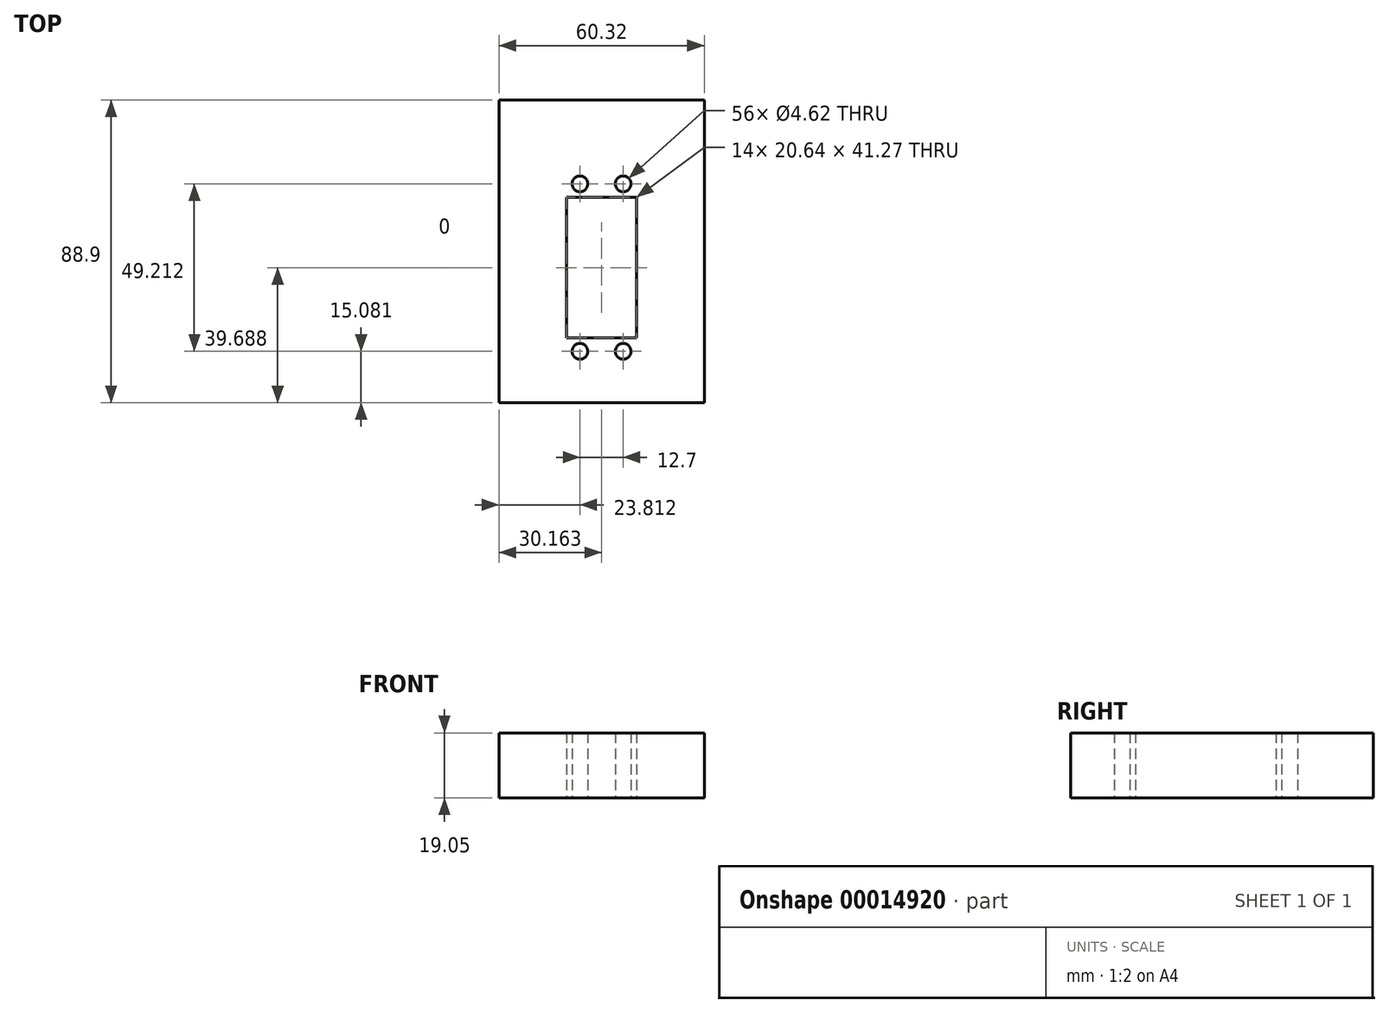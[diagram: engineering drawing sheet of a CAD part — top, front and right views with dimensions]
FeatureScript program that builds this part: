
annotation { "Feature Type Name" : "Feature", "Feature Type Description" : "" }
export const myFeature = defineFeature(function(context is Context, id is Id, definition is map)
    precondition{}
    {
        {
            var Q0;
            Q0=qCreatedBy(makeId("Top.planeOp"),FACE);
            var sketch = newSketch(context, id + "F0", { "sketchPlane" : qUnion([Q0])});
            skLineSegment(sketch, "E0.bottom", {"start": v(0, 76.2) * mm, "end": v(60.33, 76.2) * mm});
            skLineSegment(sketch, "E0.top", {"start": v(0, 0) * mm, "end": v(60.33, 0) * mm});
            skLineSegment(sketch, "E0.left", {"start": v(0, 76.2) * mm, "end": v(0, 0) * mm});
            skLineSegment(sketch, "E0.right", {"start": v(60.33, 76.2) * mm, "end": v(60.33, 0) * mm});
            skLineSegment(sketch, "E1", {"start": v(0, 76.2) * mm, "end": v(60.33, 0) * mm});
            skLineSegment(sketch, "E2", {"start": v(60.33, 76.2) * mm, "end": v(0, 0) * mm});
            skPoint(sketch, "E3", {"position": v(30.16, 38.1) * mm});
            skLineSegment(sketch, "E4.bottom", {"start": v(19.84, 47.62) * mm, "end": v(40.48, 47.62) * mm});
            skLineSegment(sketch, "E4.top", {"start": v(19.84, 6.35) * mm, "end": v(40.48, 6.35) * mm});
            skLineSegment(sketch, "E4.left", {"start": v(19.84, 47.62) * mm, "end": v(19.84, 6.35) * mm});
            skLineSegment(sketch, "E4.right", {"start": v(40.48, 47.62) * mm, "end": v(40.48, 6.35) * mm});
            skPoint(sketch, "E5", {"position": v(30.16, 47.62) * mm});
            skLineSegment(sketch, "E6", {"start": v(30.16, 38.1) * mm, "end": v(30.16, 47.62) * mm});
            skCircle(sketch, "E7", {"center": v(23.81, 2.38) * mm, "radius": 2.31 * mm});
            skCircle(sketch, "E8", {"center": v(36.51, 2.38) * mm, "radius": 2.31 * mm});
            skCircle(sketch, "E9", {"center": v(23.81, 51.6) * mm, "radius": 2.31 * mm});
            skCircle(sketch, "E10", {"center": v(36.51, 51.6) * mm, "radius": 2.31 * mm});
            skLineSegment(sketch, "E11.top", {"start": v(0, -12.7) * mm, "end": v(60.33, -12.7) * mm});
            skLineSegment(sketch, "E11.left", {"start": v(0, 0) * mm, "end": v(0, -12.7) * mm});
            skLineSegment(sketch, "E11.right", {"start": v(60.33, 0) * mm, "end": v(60.33, -12.7) * mm});
            skSolve(sketch);
        }
        {
            var Q0;
            {var subQ7=sQuery(id+"F0.wireOp",EDGE,"E0.left");Q0=makeQuery(id+"F0.imprint","IMPRINT",FACE,{"disambiguationData":[TD([[makeQuery(id+"F0.imprint","IMPRINT",EDGE,{"derivedFrom":subQ7}),1.0]])]});}
            var Q1;
            {var subQ6=sQuery(id+"F0.wireOp",EDGE,"E0.bottom");Q1=makeQuery(id+"F0.imprint","IMPRINT",FACE,{"disambiguationData":[TD([[makeQuery(id+"F0.imprint","IMPRINT",EDGE,{"derivedFrom":subQ6}),-1.0]])]});}
            var Q2;
            {var subQ5=sQuery(id+"F0.wireOp",EDGE,"E0.right");Q2=makeQuery(id+"F0.imprint","IMPRINT",FACE,{"disambiguationData":[TD([[makeQuery(id+"F0.imprint","IMPRINT",EDGE,{"derivedFrom":subQ5}),-1.0]])]});}
            var Q3;
            {var subQ7=sQuery(id+"F0.wireOp",EDGE,"E0.top");Q3=makeQuery(id+"F0.imprint","IMPRINT",FACE,{"disambiguationData":[TD([[makeQuery(id+"F0.imprint","IMPRINT",EDGE,{"derivedFrom":subQ7}),1.0]])]});}
            var Q4;
            {var subQ4=sQuery(id+"F0.wireOp",EDGE,"E4.top");Q4=makeQuery(id+"F0.imprint","IMPRINT",FACE,{"disambiguationData":[TD([[makeQuery(id+"F0.imprint","IMPRINT",EDGE,{"derivedFrom":subQ4}),-1.0]])]});}
            var Q5;
            Q5=makeQuery(id+"F0.imprint","IMPRINT",FACE,{"disambiguationData":[TD([[makeQuery(id+"F0.imprint","IMPRINT",EDGE,{"derivedFrom":sQuery(id+"F0.wireOp",EDGE,"E0.top")}),-1.0]])]});
            extrude(context, id + "F1", {"entities" : qUnion([Q0, Q1, Q2, Q3, Q4, Q5]), "depth" : 19.05 * mm});
        }
    });
